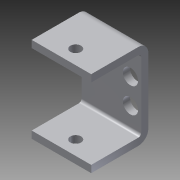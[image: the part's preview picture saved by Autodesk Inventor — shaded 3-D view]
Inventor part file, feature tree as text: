
AUTODESK INVENTOR PART (.ipt)
format: ipt  version: 2013 (Build 170138000, 138)  size: 143,360 bytes
history: native  units: in
note: dims shown in document units (in); Inventor stores cm internally (conversion verified against a paired STEP export)
features: sheet_metal_op x4, sketch x4, other x3, extrude x1
ambient origin geometry x8: Origin, YZ Plane, XZ Plane, XY Plane, X Axis, Y Axis, Z Axis, Center Point
bodies: Solid1 (feature_tree)
feature tree (12):
  sheet_metal_op  "Face1"
  sheet_metal_op  "Flange1"
  extrude  "Extrusion1"  Depth=1.15in
  sketch  "Sketch1"  dims[d4=0.5788in d5=1.15in]
  other  "Plate1"
  sketch  "Sketch2"  dims[d6=0.125in]
  other  "Plate2"
  sheet_metal_op  "Bend1"
  sheet_metal_op  "Corner1"
  sketch  "Sketch3"  dims[d7=0.125in]
  sketch  "Sketch9"  dims[d8=0.0625in d9=0.25in d10=0.125in d11=1.0in d12=90.0deg d13=0.05in d14=0.5in d15=0.125in d16=0.125in d17=0.25in d18=0.1875in d19=2999.0in d20=0.0in d21=0.575in d31=0.266in d33=0.266in d34=0.188in d35=0.125in d36=0.0in d37=0.316in d38=0.442in]
  other  "Cut4"
